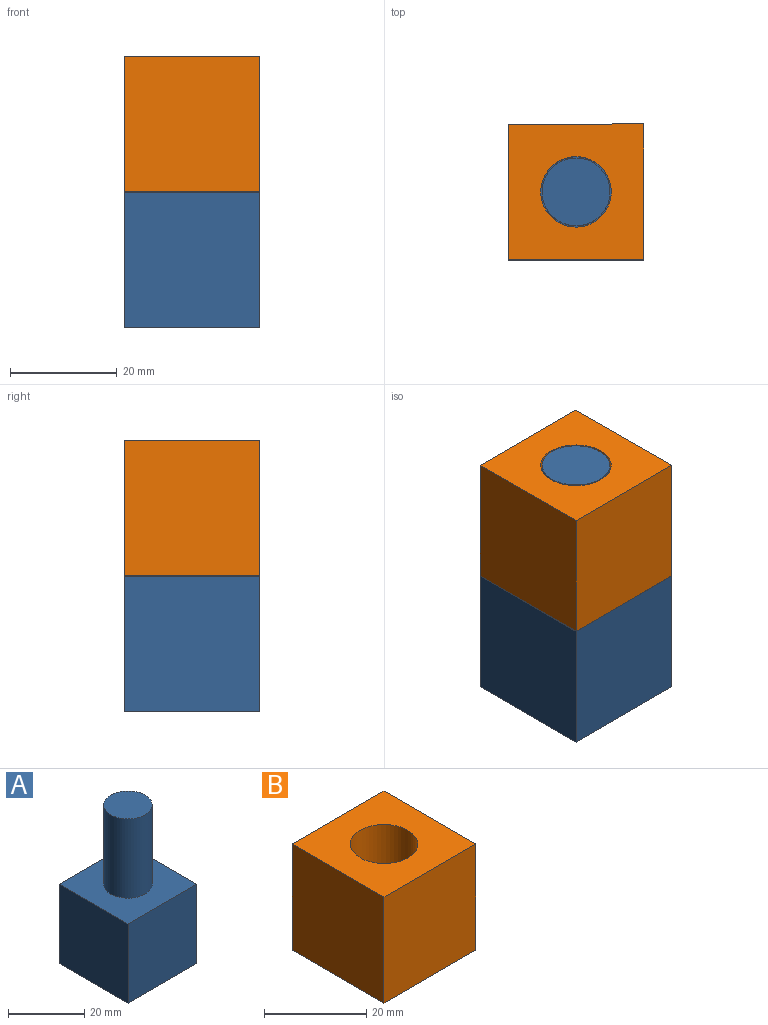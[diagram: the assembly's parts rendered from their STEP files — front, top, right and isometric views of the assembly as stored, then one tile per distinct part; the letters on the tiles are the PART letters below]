
ASSEMBLY  parts=2 mates=1
PART A: 8 faces, bbox 25.4x25.4x50.8 mm
  f0: plane 25.4x25.4mm, normal (-1,0,0), area 645.2mm2, adj f1,f3,f4,f5
  f1: plane 25.4x25.4mm, normal (0,-1,0), area 645.2mm2, adj f0,f2,f4,f5
  f2: plane 25.4x25.4mm, normal (1,0,0), area 645.2mm2, adj f1,f3,f4,f5
  f3: plane 25.4x25.4mm, normal (0,1,0), area 645.2mm2, adj f0,f2,f4,f5
  f4: plane 25.4x25.4mm, normal (0,0,1), area 518.5mm2, adj f0,f1,f2,f3,f6
  f5: plane 25.4x25.4mm, normal (0,0,-1), area 645.2mm2, adj f0,f1,f2,f3
  f6: cylinder r=6.35mm len=25.4mm, axis (0,0,-1), area 1013.4mm2, adj f4,f7
  f7: plane 12.7x12.7mm, normal (0,0,1), area 126.7mm2, adj f6
PART B: 7 faces, bbox 25.4x25.4x25.4 mm
  f0: plane 25.4x25.4mm, normal (1,0,0), area 645.2mm2, adj f1,f3,f5,f6
  f1: plane 25.4x25.4mm, normal (0,1,0), area 645.2mm2, adj f0,f2,f5,f6
  f2: plane 25.4x25.4mm, normal (-1,0,0), area 645.2mm2, adj f1,f3,f5,f6
  f3: plane 25.4x25.4mm, normal (0,-1,0), area 645.2mm2, adj f0,f2,f5,f6
  f4: cylinder r=6.6mm len=25.4mm, axis (0,0,-1), area 1054mm2, adj f5,f6
  f5: plane 25.4x25.4mm, normal (0,0,1), area 508.1mm2, adj f0,f1,f2,f3,f4
  f6: plane 25.4x25.4mm, normal (0,0,-1), area 508.1mm2, adj f0,f1,f2,f3,f4
PLACE A t=(0.58,-41.78,-6.24)mm fixed
PLACE B rot(axis=(0,0,-1),89.8deg) t=(0.58,-41.78,19.17)mm
MATE cylindrical A.f6 <-> B.f4  axis (0,0,-1) through (0.58,-41.78,31.86)mm
